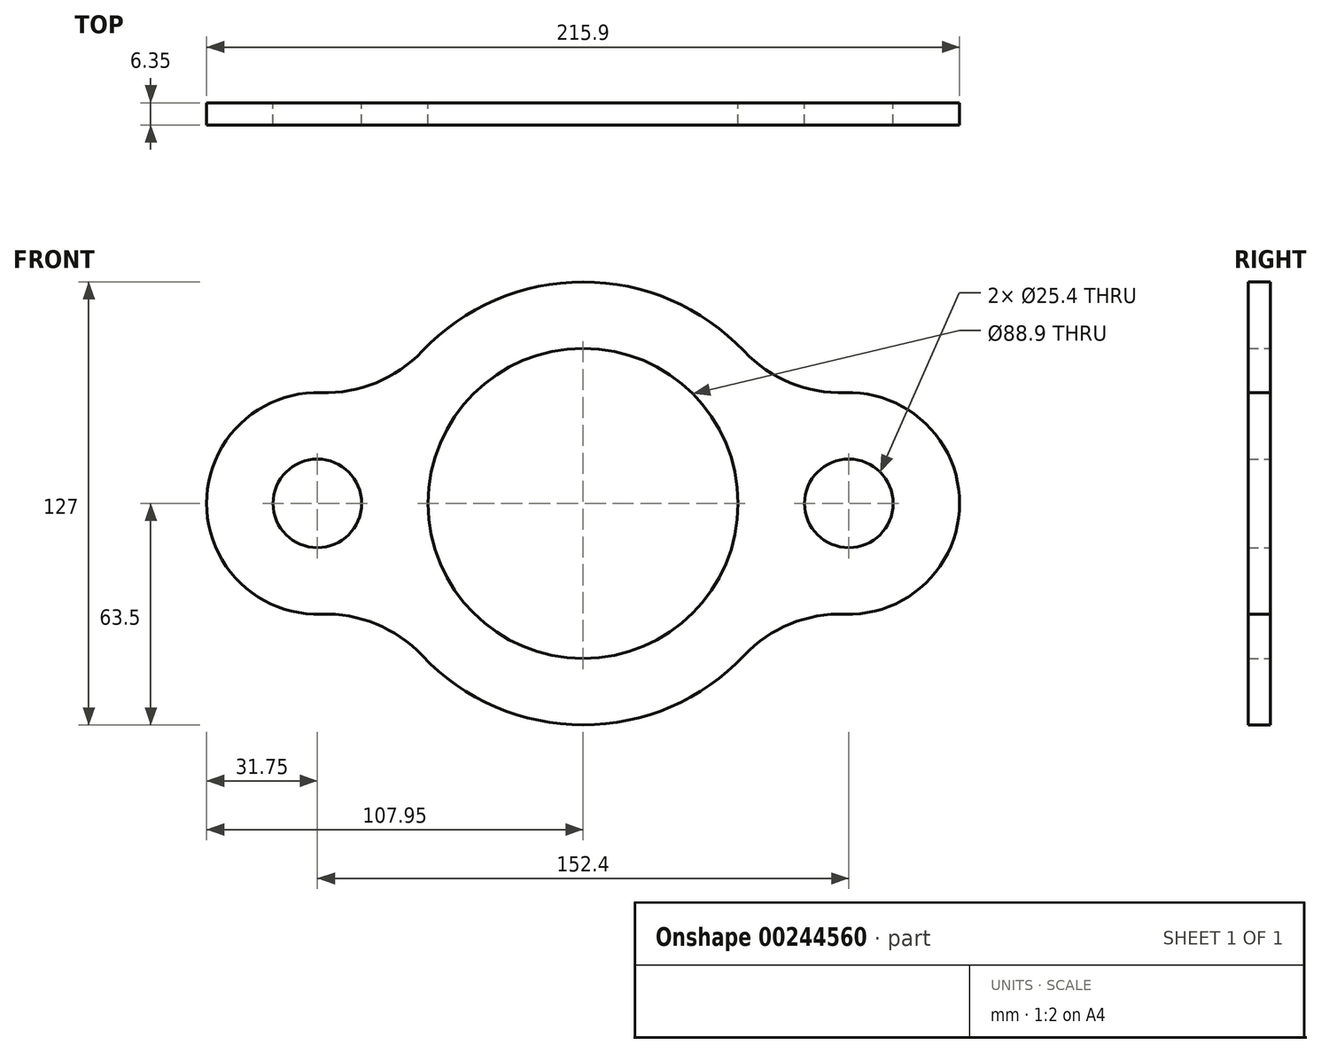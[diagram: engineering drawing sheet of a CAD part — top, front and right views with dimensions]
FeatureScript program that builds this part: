
annotation { "Feature Type Name" : "Feature", "Feature Type Description" : "" }
export const myFeature = defineFeature(function(context is Context, id is Id, definition is map)
    precondition{}
    {
        {
            var Q0;
            Q0=qCreatedBy(makeId("Front.planeOp"),FACE);
            var sketch = newSketch(context, id + "F0", { "sketchPlane" : qUnion([Q0])});
            skCircle(sketch, "E0", {"center": v(0, 0) * mm, "radius": 44.45 * mm});
            skArc(sketch, "E1", {"start": v(-46.14, -43.63) * mm, "mid": v(0, -63.5) * mm, "end": v(46.14, -43.63) * mm});
            skCircle(sketch, "E2", {"center": v(76.2, 0) * mm, "radius": 12.7 * mm});
            skArc(sketch, "E3", {"start": v(75.12, -31.73) * mm, "mid": v(107.95, 0) * mm, "end": v(75.12, 31.73) * mm});
            skCircle(sketch, "E4", {"center": v(-76.2, 0) * mm, "radius": 12.7 * mm});
            skArc(sketch, "E5", {"start": v(-75.12, 31.73) * mm, "mid": v(-107.95, 0) * mm, "end": v(-75.12, -31.73) * mm});
            skArc(sketch, "E6.trimOffspring", {"start": v(46.14, 43.63) * mm, "mid": v(0, 63.5) * mm, "end": v(-46.14, 43.63) * mm});
            skPoint(sketch, "E7.visualSharp", {"position": v(-57.94, 25.98) * mm});
            skArc(sketch, "E7.filletArc", {"start": v(-75.12, 31.73) * mm, "mid": v(-59.35, 34.56) * mm, "end": v(-46.14, 43.63) * mm});
            skPoint(sketch, "E8.visualSharp", {"position": v(57.94, 25.98) * mm});
            skArc(sketch, "E8.filletArc", {"start": v(46.14, 43.63) * mm, "mid": v(59.35, 34.56) * mm, "end": v(75.12, 31.73) * mm});
            skPoint(sketch, "E9.visualSharp", {"position": v(57.94, -25.98) * mm});
            skArc(sketch, "E9.filletArc", {"start": v(75.12, -31.73) * mm, "mid": v(59.35, -34.56) * mm, "end": v(46.14, -43.63) * mm});
            skPoint(sketch, "E10.visualSharp", {"position": v(-57.94, -25.98) * mm});
            skArc(sketch, "E10.filletArc", {"start": v(-46.14, -43.63) * mm, "mid": v(-59.35, -34.56) * mm, "end": v(-75.12, -31.73) * mm});
            skSolve(sketch);
        }
        {
            var Q0;
            Q0=makeQuery(id+"F0.imprint","IMPRINT",FACE,{"disambiguationData":[TD([[makeQuery(id+"F0.imprint","IMPRINT",EDGE,{"derivedFrom":sQuery(id+"F0.wireOp",EDGE,"E0")}),-1.0]])]});
            extrude(context, id + "F1", {"entities" : qUnion([Q0]), "depth" : 6.35 * mm});
        }
    });
